# Revit family: Mounting Brackets PNHR-096
name_source: partatom
category: Generic Models
revit_build: Autodesk Revit 2017 (Build: 20190508_0315(x64)
units: mm (PartAtom-declared; Revit-internal decimal feet)

## family parameters
Always vertical = No
Can host rebar = No
Cut with Voids When Loaded = No
Part Type = Normal
Room Calculation Point = No
Round Connector Dimension = Use Diameter
Shared = No
Work Plane-Based = Yes

## types (5) — shared parameters
Assembly Code = 63.0
Bolt_Material = Brass, Soft Yellow, Welded
Bolt_Visibility = No
Bracket Article Number = *User Defined
Bracket_Width = 18 mm
Default Elevation = 1219 mm
Description = Mounting Brackets
Find - Bracket Article Number = https://www.veko.com
Manufacturer = Veko Lightsystems
Mounting_Material = Aluminum 7175 T73 0 Hot Formed
Pendulum Visibility = No

## per-type parameters (varying)
| type | B14 | B24 | B35 | B35-C | BSK | Pendulum Start |
| B14 | Yes | No | No | No | No | 47 mm |
| B24 | No | Yes | No | No | No | 90 mm |
| BSK | No | No | No | No | Yes | 73 mm |
| B35 | No | No | Yes | No | No | 49 mm |
| B35-C | No | No | No | Yes | No | 49 mm |

note: column(s) folded — value = type name in every type: Model

## geometry (parser evidence)
native form markers: Sweep x5
no freeform markers — native parametric forms only
